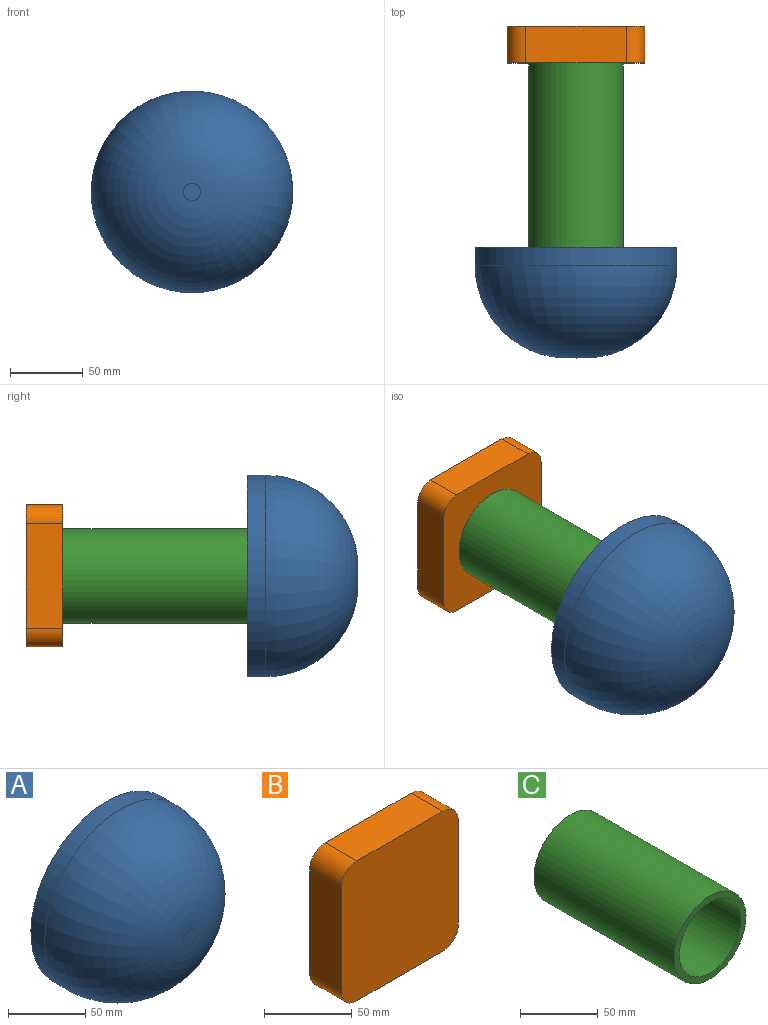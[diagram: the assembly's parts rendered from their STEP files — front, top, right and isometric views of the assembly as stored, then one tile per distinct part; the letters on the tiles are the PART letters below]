
ASSEMBLY  parts=3 mates=2
PART A: 4 faces, bbox 138.9x76.2x138.9 mm
  f0: cylinder r=69.44mm len=138.88mm, axis (0,1,0), area 5541mm2, adj f2,f3
  f1: plane 11.88x11.88mm, normal (0,-1,0), area 110.8mm2, adj f3
  f2: plane 138.88x138.88mm, normal (0,1,0), area 15148.4mm2, adj f0
  f3: torus R=5.94mm, axis (0,-1,0), area 29057.9mm2, adj f0,f1
PART B: 10 faces, bbox 94.6x25.4x97.7 mm
  f0: plane 72.31x25.4mm, normal (-1,0,0), area 1836.7mm2, adj f4,f5,f7,f8
  f1: plane 69.22x25.4mm, normal (0,0,-1), area 1758.2mm2, adj f4,f5,f8,f9
  f2: plane 72.31x25.4mm, normal (1,0,0), area 1836.7mm2, adj f4,f5,f6,f9
  f3: plane 69.22x25.4mm, normal (0,0,1), area 1758.2mm2, adj f4,f5,f6,f7
  f4: plane 97.71x94.62mm, normal (0,-1,0), area 9106.8mm2, adj f0,f1,f2,f3,f6,f7,f8,f9
  f5: plane 97.71x94.62mm, normal (0,1,0), area 9106.8mm2, adj f0,f1,f2,f3,f6,f7,f8,f9
  f6: cylinder r=12.7mm len=25.4mm, axis (0,-1,0), area 506.7mm2, adj f2,f3,f4,f5
  f7: cylinder r=12.7mm len=25.4mm, axis (0,1,0), area 506.7mm2, adj f0,f3,f4,f5
  f8: cylinder r=12.7mm len=25.4mm, axis (0,-1,0), area 506.7mm2, adj f0,f1,f4,f5
  f9: cylinder r=12.7mm len=25.4mm, axis (0,1,0), area 506.7mm2, adj f1,f2,f4,f5
PART C: 4 faces, bbox 65.3x127x65.3 mm
  f0: cylinder r=27.86mm len=127mm, axis (0,1,0), area 22230.5mm2, adj f2,f3
  f1: cylinder r=32.66mm len=127mm, axis (0,1,0), area 26062mm2, adj f2,f3
  f2: plane 65.32x65.32mm, normal (0,-1,0), area 912.9mm2, adj f0,f1
  f3: plane 65.32x65.32mm, normal (0,1,0), area 912.9mm2, adj f0,f1
PLACE A t=(15.46,-102.49,58.35)mm
PLACE B t=(15.46,49.91,58.35)mm
PLACE C t=(15.46,24.51,58.35)mm
MATE parallel A.f0 <-> C.f0  axis (0,-1,0) through (15.46,-102.49,58.35)mm
MATE parallel B.f4 <-> C.f1  axis (0,-1,0) through (15.46,24.51,58.35)mm
